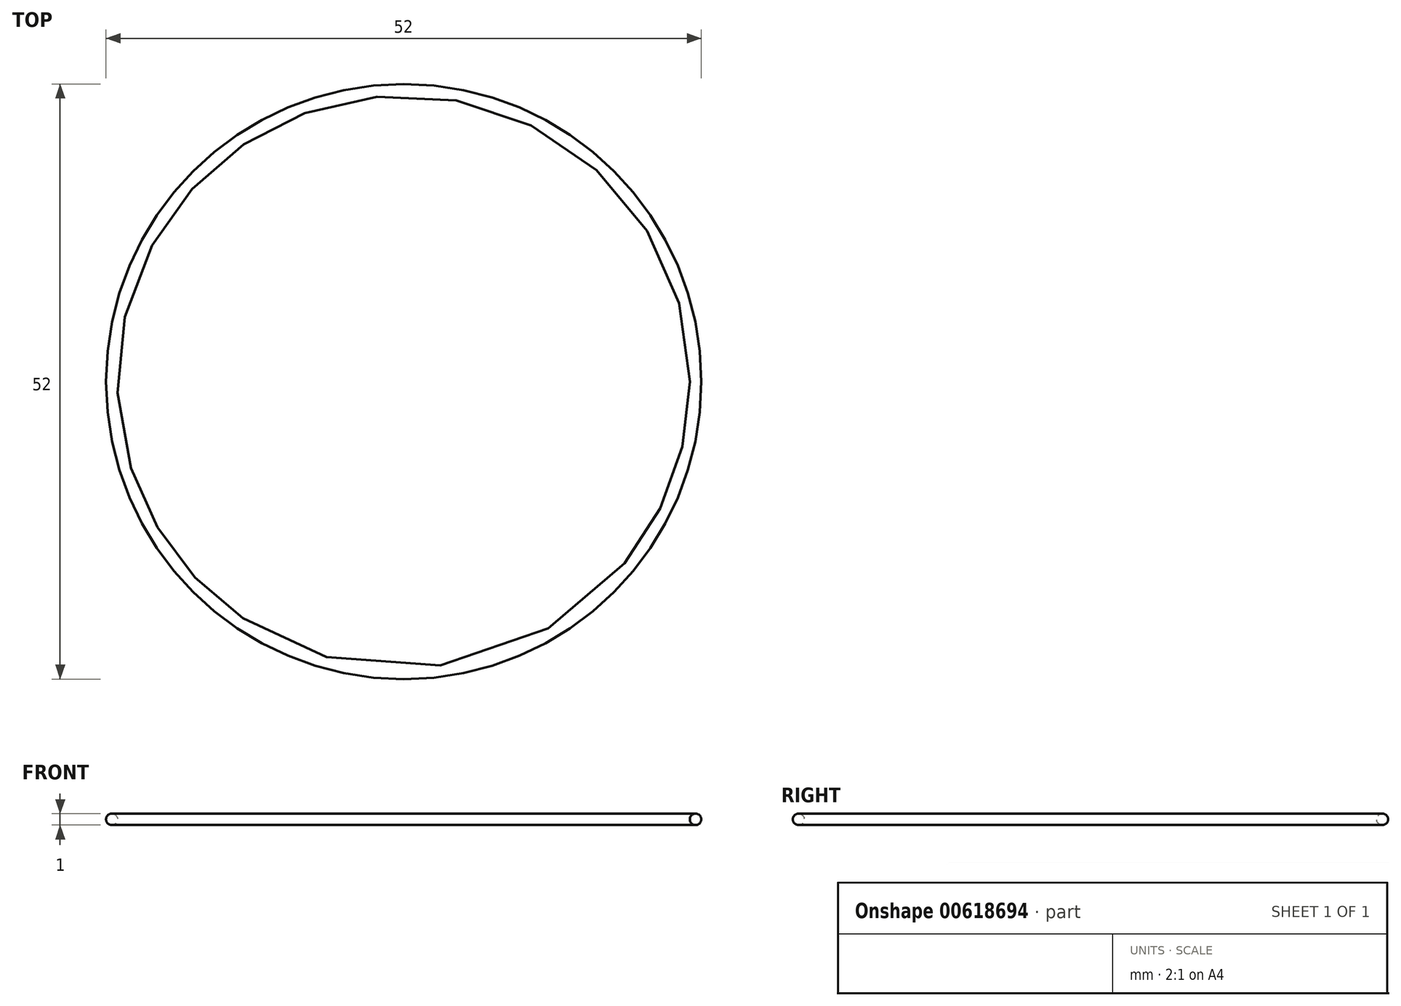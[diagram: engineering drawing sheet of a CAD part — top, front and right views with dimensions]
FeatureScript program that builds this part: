
annotation { "Feature Type Name" : "Feature", "Feature Type Description" : "" }
export const myFeature = defineFeature(function(context is Context, id is Id, definition is map)
    precondition{}
    {
        {
            var Q0;
            Q0=qCreatedBy(makeId("Front.planeOp"),FACE);
            var sketch = newSketch(context, id + "F0", { "sketchPlane" : qUnion([Q0])});
            skCircle(sketch, "E0", {"center": v(-25.5, 0) * mm, "radius": 0.5 * mm});
            skSolve(sketch);
        }
        {
            var Q0;
            Q0=qCreatedBy(makeId("Front.planeOp"),FACE);
            var sketch = newSketch(context, id + "F1", { "sketchPlane" : qUnion([Q0])});
            skLineSegment(sketch, "E1", {"start": v(0, 27.83) * mm, "end": v(0, -27.34) * mm, "construction": true});
            skSolve(sketch);
        }
        {
            var Q0;
            Q0=makeQuery(id+"F0.imprint","IMPRINT",FACE,{"disambiguationData":[TD([[makeQuery(id+"F0.imprint","IMPRINT",EDGE,{"derivedFrom":sQuery(id+"F0.wireOp",EDGE,"E0")}),1.0]])]});
            var Q1;
            Q1=sQuery(id+"F1.wireOp",EDGE,"E1");
            revolve(context, id + "F2", {"surfaceOperationType" : NewSurfaceOperationType.NEW, "entities" : qUnion([Q0]), "axis" : qUnion([Q1]), "revolveType" : RevolveType.FULL});
        }
    });
